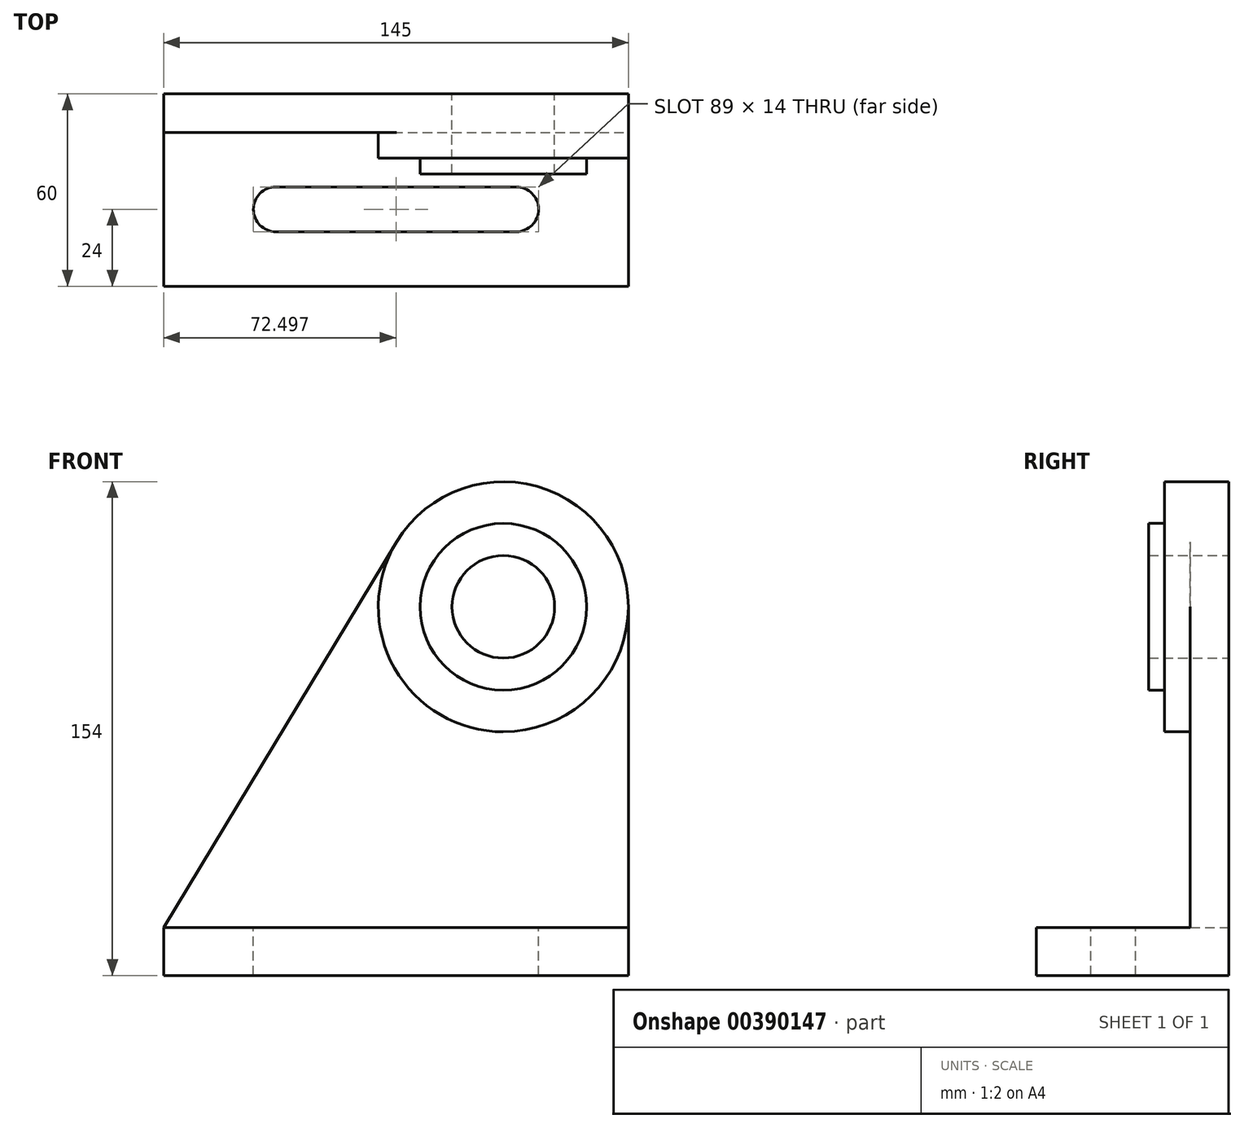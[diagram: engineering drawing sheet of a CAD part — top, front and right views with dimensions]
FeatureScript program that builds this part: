
annotation { "Feature Type Name" : "Feature", "Feature Type Description" : "" }
export const myFeature = defineFeature(function(context is Context, id is Id, definition is map)
    precondition{}
    {
        {
            var Q0;
            Q0=qCreatedBy(makeId("Front.planeOp"),FACE);
            var sketch = newSketch(context, id + "F0", { "sketchPlane" : qUnion([Q0])});
            skLineSegment(sketch, "E0", {"start": v(-82.77, -60.98) * mm, "end": v(62.23, -60.98) * mm});
            skLineSegment(sketch, "E1", {"start": v(62.23, -60.98) * mm, "end": v(62.23, 54.02) * mm});
            skLineSegment(sketch, "E2", {"start": v(62.23, 54.02) * mm, "end": v(-15.77, 54.02) * mm, "construction": true});
            skCircle(sketch, "E3", {"center": v(23.23, 54.02) * mm, "radius": 39 * mm});
            skLineSegment(sketch, "E4", {"start": v(23.23, 93.02) * mm, "end": v(23.23, 15.02) * mm, "construction": true});
            skCircle(sketch, "E5", {"center": v(23.23, 54.02) * mm, "radius": 26 * mm});
            skCircle(sketch, "E6", {"center": v(23.23, 54.02) * mm, "radius": 16 * mm});
            skLineSegment(sketch, "E7", {"start": v(-82.77, -60.98) * mm, "end": v(-82.77, -45.98) * mm});
            skLineSegment(sketch, "E8", {"start": v(-82.77, -45.98) * mm, "end": v(62.23, -45.98) * mm});
            skLineSegment(sketch, "E9", {"start": v(-82.77, -45.98) * mm, "end": v(-10.15, 74.19) * mm});
            skSolve(sketch);
        }
        {
            var Q0;
            Q0=makeQuery(id+"F0.imprint","IMPRINT",FACE,{"disambiguationData":[TD([[makeQuery(id+"F0.imprint","IMPRINT",EDGE,{"derivedFrom":sQuery(id+"F0.wireOp",EDGE,"E5")}),1.0]])]});
            extrude(context, id + "F1", {"entities" : qUnion([Q0]), "depth" : 25 * mm});
        }
        {
            var Q0;
            Q0=makeQuery(id+"F0.imprint","IMPRINT",FACE,{"disambiguationData":[TD([[makeQuery(id+"F0.imprint","IMPRINT",EDGE,{"derivedFrom":sQuery(id+"F0.wireOp",EDGE,"E5")}),-1.0]])]});
            extrude(context, id + "F2", {"entities" : qUnion([Q0]), "operationType" : NewBodyOperationType.ADD, "depth" : 20 * mm});
        }
        {
            var Q0;
            {var subQ3=sQuery(id+"F0.wireOp",EDGE,"E8");Q0=makeQuery(id+"F0.imprint","IMPRINT",FACE,{"disambiguationData":[TD([[makeQuery(id+"F0.imprint","IMPRINT",EDGE,{"derivedFrom":subQ3}),1.0]])]});}
            extrude(context, id + "F3", {"entities" : qUnion([Q0]), "operationType" : NewBodyOperationType.ADD, "depth" : 12 * mm});
        }
        {
            var Q0;
            {var subQ0=sQuery(id+"F0.wireOp",EDGE,"E0");Q0=makeQuery(id+"F0.imprint","IMPRINT",FACE,{"disambiguationData":[TD([[makeQuery(id+"F0.imprint","IMPRINT",EDGE,{"derivedFrom":subQ0}),1.0]])]});}
            extrude(context, id + "F4", {"entities" : qUnion([Q0]), "operationType" : NewBodyOperationType.ADD, "depth" : 60 * mm});
        }
        {
            var Q0;
            Q0=makeQuery(id+"F4.opExtrude","SWEPT_FACE",FACE,{"disambiguationData":[OSD([sQuery(id+"F0.wireOp",EDGE,"E8")])]});
            var sketch = newSketch(context, id + "F5", { "sketchPlane" : qUnion([Q0])});
            skLineSegment(sketch, "E10", {"start": v(-54.77, -36) * mm, "end": v(-40.77, -36) * mm, "construction": true});
            skLineSegment(sketch, "E11", {"start": v(-47.77, -43) * mm, "end": v(-47.77, -29) * mm, "construction": true});
            skArc(sketch, "E12", {"start": v(-47.77, -29) * mm, "mid": v(-54.77, -36) * mm, "end": v(-47.77, -43) * mm});
            skLineSegment(sketch, "E13", {"start": v(27.23, -43) * mm, "end": v(27.23, -29) * mm, "construction": true});
            skArc(sketch, "E14", {"start": v(27.23, -43) * mm, "mid": v(34.23, -36) * mm, "end": v(27.23, -29) * mm});
            skPoint(sketch, "E15.orphan", {"position": v(-82.77, -36) * mm});
            skLineSegment(sketch, "E16.trimOffspring", {"start": v(20.23, -36) * mm, "end": v(34.23, -36) * mm, "construction": true});
            skLineSegment(sketch, "E17", {"start": v(-47.77, -29) * mm, "end": v(27.23, -29) * mm});
            skLineSegment(sketch, "E18", {"start": v(-47.77, -43) * mm, "end": v(27.23, -43) * mm});
            skSolve(sketch);
        }
        {
            var Q0;
            Q0=makeQuery(id+"F5.imprint","IMPRINT",FACE,{"disambiguationData":[TD([[makeQuery(id+"F5.imprint","IMPRINT",EDGE,{"derivedFrom":sQuery(id+"F5.wireOp",EDGE,"E12")}),1.0]])]});
            extrude(context, id + "F6", {"entities" : qUnion([Q0]), "operationType" : NewBodyOperationType.REMOVE, "oppositeDirection" : true, "depth" : 25 * mm});
        }
    });
